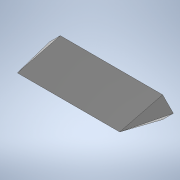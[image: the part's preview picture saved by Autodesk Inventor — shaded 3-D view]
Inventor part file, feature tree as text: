
AUTODESK INVENTOR PART (.ipt)
format: ipt  version: 2020 (Build 240168000, 168)  size: 310,784 bytes
history: native  units: in
note: dims shown in document units (in); Inventor stores cm internally (conversion verified against a paired STEP export)
features: extrude x8, sketch x8, projected_geometry x8, plane x2, mirror x1
ambient origin geometry x8: Origin, YZ Plane, XZ Plane, XY Plane, X Axis, Y Axis, Z Axis, Center Point
bodies: Body1 (feature_tree)
feature tree (27):
  extrude  "Extrusion24"  Depth=2.3622in
  extrude  "Extrusion25"  TaperAngle=0.0deg  [1 undecoded]
  plane  "Work Plane14"
  plane  "Work Plane15"
  extrude  "Extrusion26"  Depth=0.5906in
  extrude  "Extrusion27"  Depth=0.3484in TaperAngle=0.0deg
  mirror  "Mirror11"
  extrude  "Extrusion28"  Depth=4.3307in
  extrude  "Extrusion29"  Depth=0.2756in
  extrude  "Extrusion30"  Depth=0.2362in
  extrude  "Extrusion31"  Depth=0.3937in
  sketch  "Sketch29"  dims[d121=1.1811in d122=2.3622in]
  sketch  "Sketch30"  dims[d123=5.6307in d124=0.0in]
  projected_geometry  "Projected Loop15"
  sketch  "Sketch31"  dims[d125=0.5906in d126=5.6307in]
  sketch  "Sketch32"  dims[d127=0.0in d128=0.3484in d129=0.0in]
  sketch  "Sketch33"  dims[d130=0.9559in d131=0.0in d132=4.3307in]
  sketch  "Sketch34"  dims[d133=1.0005in d140=0.2756in]
  projected_geometry  "Projected Loop16"
  sketch  "Sketch36"  dims[d141=0.0in d142=0.2362in]
  projected_geometry  "Projected Loop23"
  projected_geometry  "Projected Loop24"
  sketch  "Sketch37"  dims[d143=0.2362in d144=0.1142in d145=0.1142in d146=0.1142in d147=0.1142in d148=0.1181in d149=0.1575in d150=0.1575in d151=0.1378in d152=0.0in d153=0.3937in d154=-0.3092in d155=0.3937in d156=-0.3092in d50=0.0197in d51=0.0344in d52=0.0197in d53=0.0344in d73=0.0197in d74=0.0344in d75=0.0197in d76=0.0344in]
  projected_geometry  "Projected Loop25"
  projected_geometry  "Projected Loop26"
  projected_geometry  "Projected Loop27"
  projected_geometry  "Projected Loop28"
note: 1 required parameter value undecoded (feature->parameter linkage not recoverable at this tier; creation-order binding heuristic only, values carry confidence <= 0.55)
